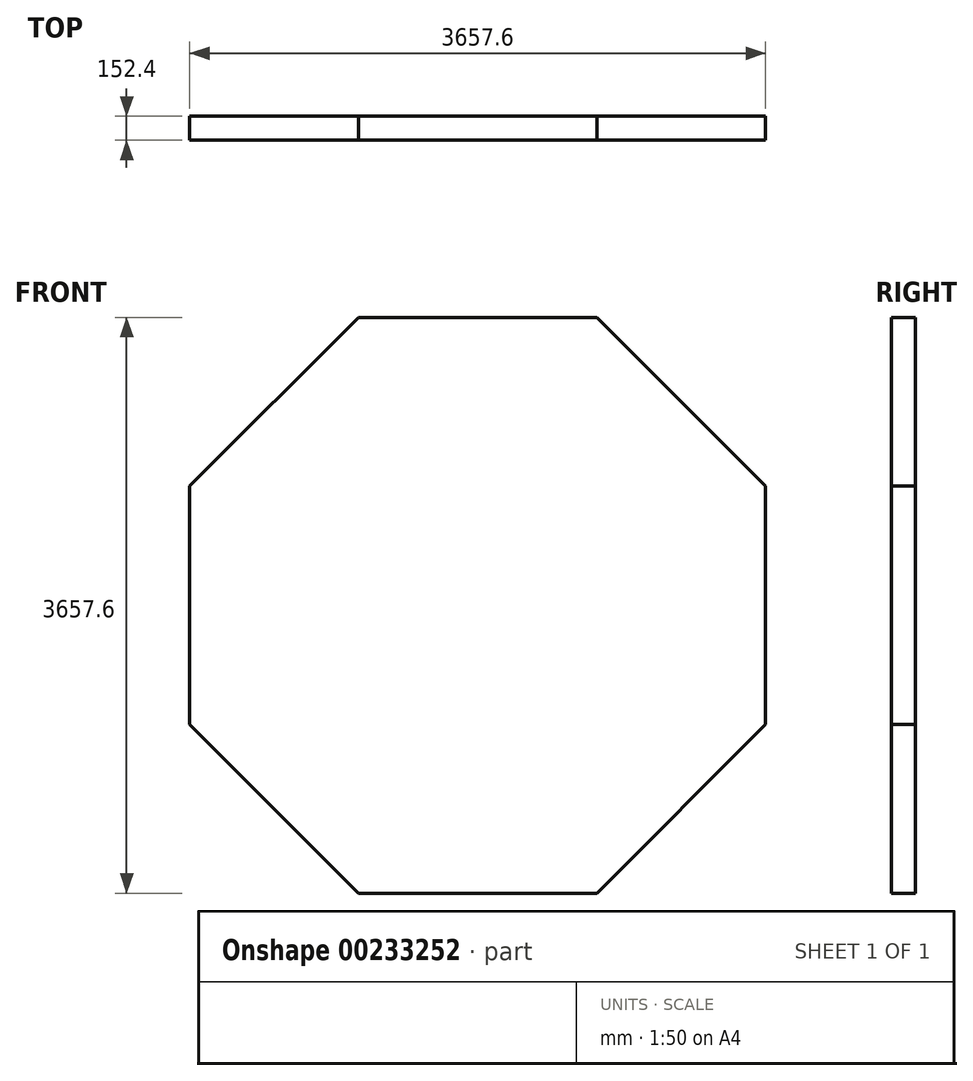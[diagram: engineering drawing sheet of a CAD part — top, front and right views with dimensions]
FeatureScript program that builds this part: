
annotation { "Feature Type Name" : "Feature", "Feature Type Description" : "" }
export const myFeature = defineFeature(function(context is Context, id is Id, definition is map)
    precondition{}
    {
        {
            var Q0;
            Q0=qCreatedBy(makeId("Front.planeOp"),FACE);
            var sketch = newSketch(context, id + "F0", { "sketchPlane" : qUnion([Q0])});
            skCircle(sketch, "E0.cCircle", {"center": v(0, 0) * mm, "radius": 1828.8 * mm, "construction": true});
            skLineSegment(sketch, "E0.0", {"start": v(-757.51, 1828.8) * mm, "end": v(757.51, 1828.8) * mm});
            skLineSegment(sketch, "E0.1", {"start": v(757.51, 1828.8) * mm, "end": v(1828.8, 757.51) * mm});
            skLineSegment(sketch, "E0.2", {"start": v(1828.8, 757.51) * mm, "end": v(1828.8, -757.51) * mm});
            skLineSegment(sketch, "E0.3", {"start": v(1828.8, -757.51) * mm, "end": v(757.51, -1828.8) * mm});
            skLineSegment(sketch, "E0.4", {"start": v(757.51, -1828.8) * mm, "end": v(-757.51, -1828.8) * mm});
            skLineSegment(sketch, "E0.5", {"start": v(-757.51, -1828.8) * mm, "end": v(-1828.8, -757.51) * mm});
            skLineSegment(sketch, "E0.6", {"start": v(-1828.8, -757.51) * mm, "end": v(-1828.8, 757.51) * mm});
            skLineSegment(sketch, "E0.7", {"start": v(-1828.8, 757.51) * mm, "end": v(-757.51, 1828.8) * mm});
            skPoint(sketch, "E0.0.midPoint", {"position": v(0, 1828.8) * mm});
            skSolve(sketch);
        }
        {
            var Q0;
            Q0 = qSketchRegion(id + "F0", true);
            extrude(context, id + "F1", {"entities" : qUnion([Q0]), "depth" : 152.4 * mm});
        }
    });
